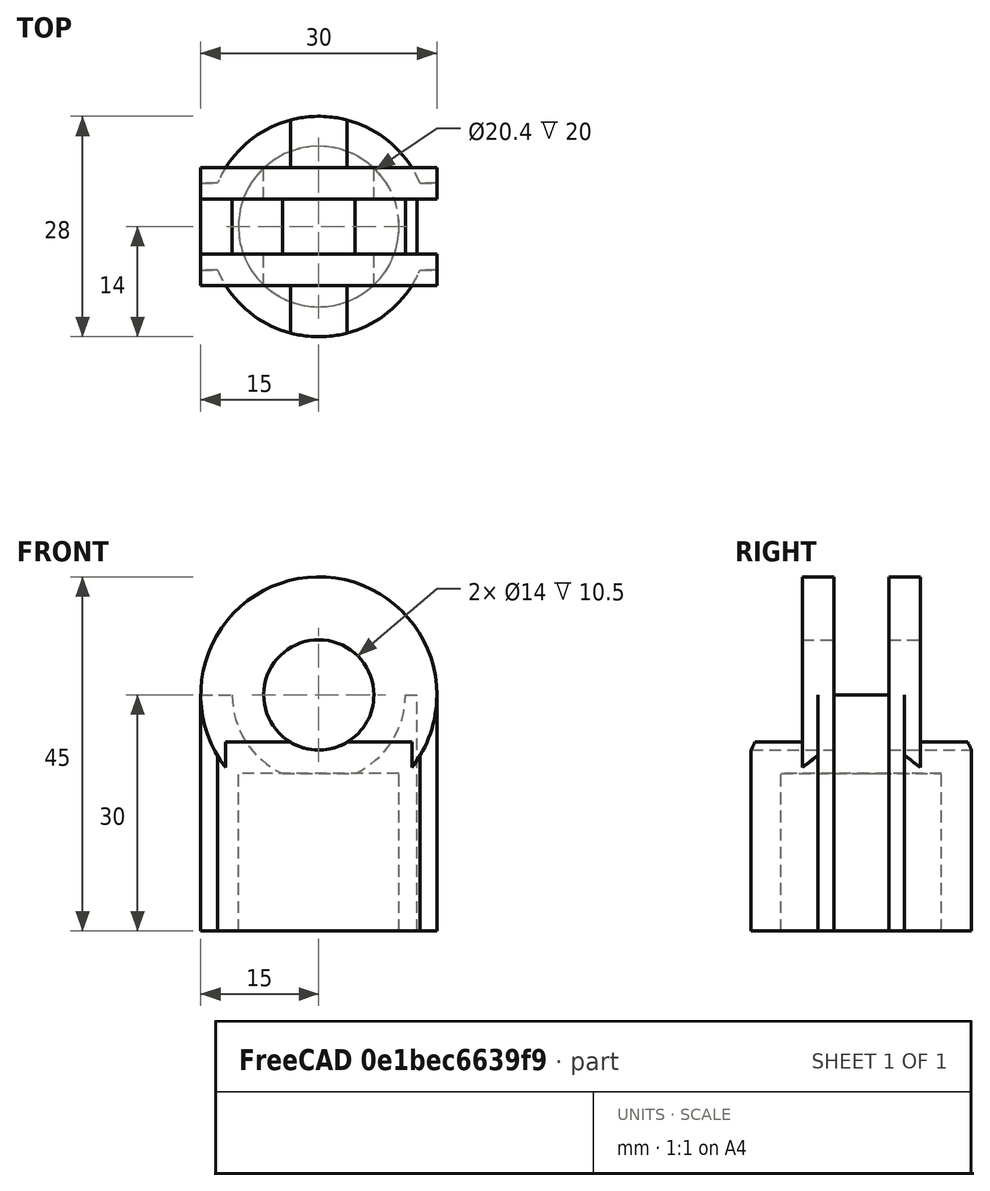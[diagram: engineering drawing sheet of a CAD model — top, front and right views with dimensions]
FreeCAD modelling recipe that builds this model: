
FCSTD DOCUMENT  (FreeCAD 0.17R13522 (Git))
Label: connector-bearing
License: All rights reserved
LicenseURL: http://en.wikipedia.org/wiki/All_rights_reserved
objects: Part::Cylinder×5, Part::Box×3, Part::MultiFuse×2, Part::Cut×1
note: 11 computed .brp shape members not serialized (recipe doc carries the construction recipe); baked Part::Feature solids carry a one-line shape summary decoded from their .brp

FEATURE [Part::Cylinder] Cylinder
  Angle = 360
  AttacherType = Attacher::AttachEngine3D
  Height = 24
  Radius = 14
FEATURE [Part::Cylinder] Cylinder001
  Angle = 360
  AttacherType = Attacher::AttachEngine3D
  Height = 15
  Placement = pos=(0,-7.5,30) rot=(1,0,0;4.71239rad)
  Radius = 15
FEATURE [Part::Cylinder] Cylinder002
  Angle = 360
  AttacherType = Attacher::AttachEngine3D
  Height = 7
  Placement = pos=(0,-3.5,30) rot=(-1,0,0;1.5708rad)
  Radius = 11
FEATURE [Part::Cylinder] Cylinder004
  Angle = 360
  AttacherType = Attacher::AttachEngine3D
  Height = 30
  Placement = pos=(0,-15,30) rot=(-1,0,0;1.5708rad)
  Radius = 7
FEATURE [Part::Box] Box  label="Cube"
  AttacherType = Attacher::AttachEngine3D
  Height = 15
  Length = 30
  Placement = pos=(-15,-3.5,30) rot=(0,0,1;0rad)
  Width = 7
FEATURE [Part::Box] Box001  label="Cube001"
  AttacherType = Attacher::AttachEngine3D
  Height = 30
  Length = 10
  Placement = pos=(12.5,-3.5,0) rot=(0,0,1;0rad)
  Width = 7
FEATURE [Part::Box] Box002  label="Cube002"
  AttacherType = Attacher::AttachEngine3D
  Height = 30
  Length = 30
  Placement = pos=(-15,-5.5,0) rot=(0,0,1;0rad)
  Width = 11
FEATURE [Part::MultiFuse] Fusion  label="Positive Fusion"
  Shapes = -> [Cylinder,Cylinder001,Box002]
FEATURE [Part::Cylinder] Cylinder005
  Angle = 360
  AttacherType = Attacher::AttachEngine3D
  Height = 20
  Radius = 10.2
FEATURE [Part::MultiFuse] Fusion001  label="Negative Fustion"
  Shapes = -> [Cylinder004,Cylinder002,Box,Box001,Cylinder005]
FEATURE [Part::Cut] Cut
  Base = -> Fusion
  Tool = -> Fusion001
